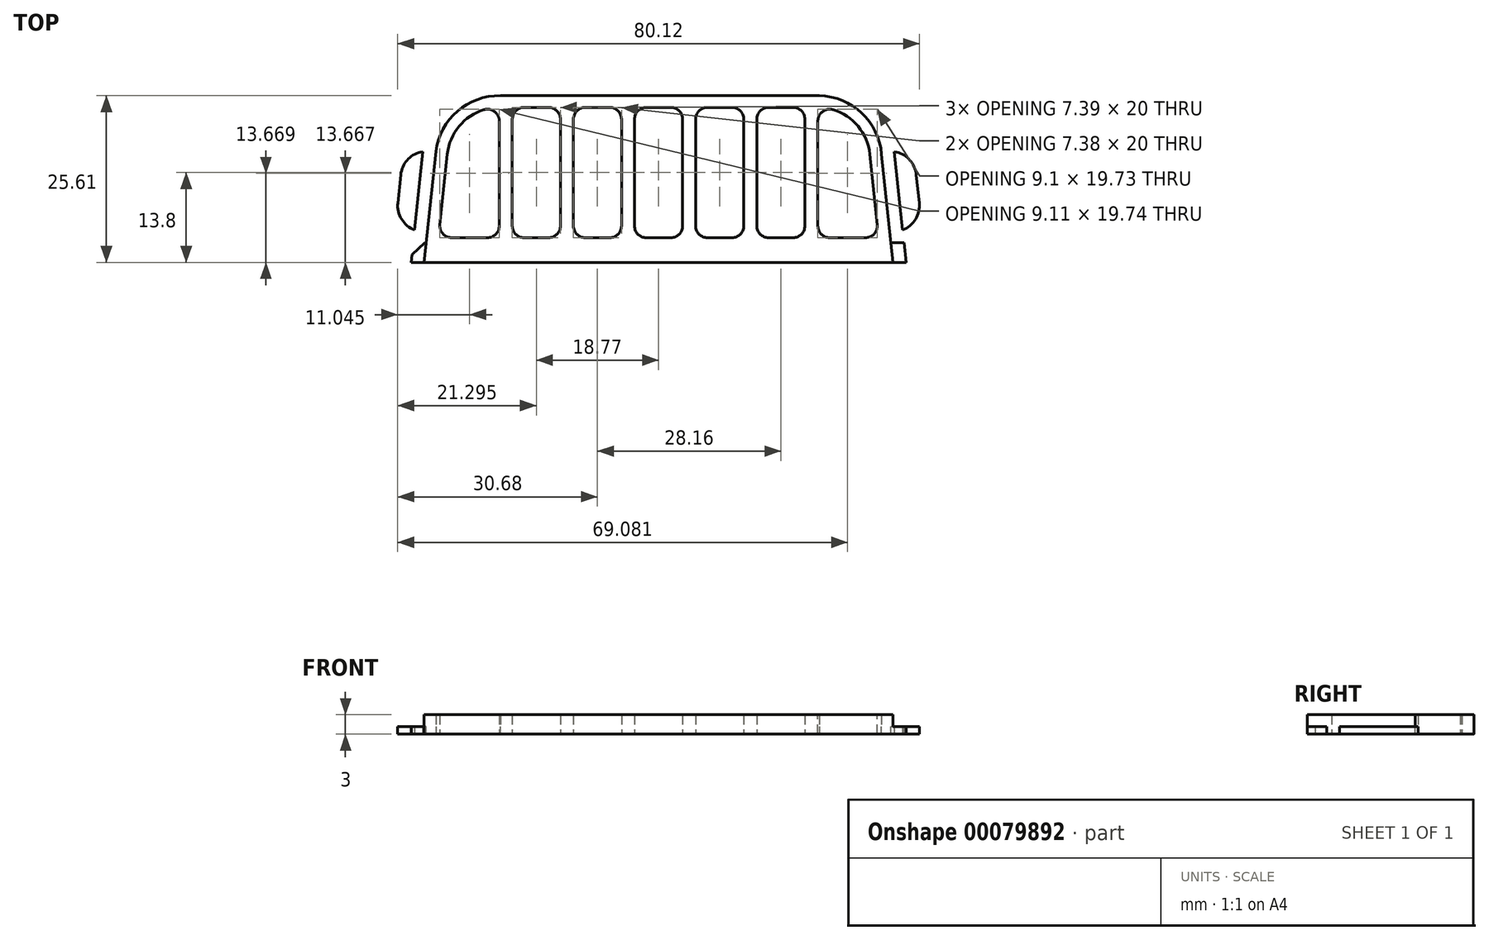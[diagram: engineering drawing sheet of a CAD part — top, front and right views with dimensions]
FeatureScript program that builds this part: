
annotation { "Feature Type Name" : "Feature", "Feature Type Description" : "" }
export const myFeature = defineFeature(function(context is Context, id is Id, definition is map)
    precondition{}
    {
        {
            var Q0;
            Q0=qCreatedBy(makeId("Top.planeOp"),FACE);
            var sketch = newSketch(context, id + "F0", { "sketchPlane" : qUnion([Q0])});
            skLineSegment(sketch, "E0", {"start": v(-36, 0) * mm, "end": v(36, 0) * mm});
            skLineSegment(sketch, "E1", {"start": v(-36, 24) * mm, "end": v(38.4, 24) * mm, "construction": true});
            skPoint(sketch, "E2", {"position": v(0, 0) * mm});
            skLineSegment(sketch, "E3", {"start": v(-36, 0) * mm, "end": v(-34.42, 15.05) * mm});
            skLineSegment(sketch, "E4.MirrorCS", {"start": v(36, 0) * mm, "end": v(34.42, 15.05) * mm});
            skLineSegment(sketch, "E5", {"start": v(24.47, 24) * mm, "end": v(-24.47, 24) * mm});
            skPoint(sketch, "E6.visualSharp", {"position": v(33.48, 24) * mm});
            skArc(sketch, "E6.filletArc", {"start": v(34.42, 15.05) * mm, "mid": v(31.16, 21.43) * mm, "end": v(24.47, 24) * mm});
            skPoint(sketch, "E7.visualSharp", {"position": v(-33.48, 24) * mm});
            skArc(sketch, "E7.filletArc", {"start": v(-24.47, 24) * mm, "mid": v(-31.16, 21.43) * mm, "end": v(-34.42, 15.05) * mm});
            skSolve(sketch);
        }
        {
            var Q0;
            Q0=qCreatedBy(makeId("Top.planeOp"),FACE);
            var sketch = newSketch(context, id + "F1", { "sketchPlane" : qUnion([Q0])});
            skArc(sketch, "E8.0", {"start": v(36.2, 15.23) * mm, "mid": v(32.37, 22.77) * mm, "end": v(24.47, 25.8) * mm});
            skArc(sketch, "E8.1", {"start": v(-24.47, 25.8) * mm, "mid": v(-32.37, 22.77) * mm, "end": v(-36.2, 15.23) * mm});
            skLineSegment(sketch, "E8.2", {"start": v(-38, -1.8) * mm, "end": v(-36.2, 15.23) * mm});
            skLineSegment(sketch, "E8.3", {"start": v(24.47, 25.8) * mm, "end": v(-24.47, 25.8) * mm});
            skLineSegment(sketch, "E8.4", {"start": v(-38, -1.8) * mm, "end": v(38, -1.8) * mm});
            skLineSegment(sketch, "E8.5", {"start": v(38, -1.8) * mm, "end": v(36.2, 15.23) * mm});
            skSolve(sketch);
        }
        {
            var Q0;
            Q0=makeQuery(id+"F1.imprint","IMPRINT",FACE,{"disambiguationData":[TD([[makeQuery(id+"F1.imprint","IMPRINT",EDGE,{"derivedFrom":sQuery(id+"F1.wireOp",EDGE,"E8.0")}),1.0]])]});
            extrude(context, id + "F2", {"entities" : qUnion([Q0]), "depth" : 3 * mm});
        }
        {
            var Q0;
            Q0=makeQuery(id+"F2.opExtrude","SWEPT_FACE",FACE,{"disambiguationData":[OSD([sQuery(id+"F1.wireOp",EDGE,"E8.4")])]});
            var sketch = newSketch(context, id + "F3", { "sketchPlane" : qUnion([Q0])});
            skLineSegment(sketch, "E9.bottom", {"start": v(-38, 3) * mm, "end": v(-36, 3) * mm});
            skLineSegment(sketch, "E9.top", {"start": v(-38, 1.2) * mm, "end": v(-36, 1.2) * mm});
            skLineSegment(sketch, "E9.left", {"start": v(-38, 3) * mm, "end": v(-38, 1.2) * mm});
            skLineSegment(sketch, "E9.right", {"start": v(-36, 3) * mm, "end": v(-36, 1.2) * mm});
            skLineSegment(sketch, "E10.0", {"start": v(-36, 0) * mm, "end": v(-34.42, 0) * mm});
            skPoint(sketch, "E11", {"position": v(-38, 1.5) * mm});
            skSolve(sketch);
        }
        {
            var Q0;
            Q0=makeQuery(id+"F3.imprint","IMPRINT",FACE,{"disambiguationData":[TD([[makeQuery(id+"F3.imprint","IMPRINT",EDGE,{"derivedFrom":sQuery(id+"F3.wireOp",EDGE,"E9.bottom")}),-1.0]])]});
            var Q1;
            Q1=makeQuery(id+"F2.opExtrude","CAP_EDGE",EDGE,{"disambiguationData":[OSD([sQuery(id+"F1.wireOp",EDGE,"E8.2")])],"isStart":false});
            var Q2;
            Q2=makeQuery(id+"F2.opExtrude","CAP_EDGE",EDGE,{"disambiguationData":[OSD([sQuery(id+"F1.wireOp",EDGE,"E8.1")])],"isStart":false});
            var Q3;
            Q3=makeQuery(id+"F2.opExtrude","CAP_EDGE",EDGE,{"disambiguationData":[OSD([sQuery(id+"F1.wireOp",EDGE,"E8.3")])],"isStart":false});
            var Q4;
            Q4=makeQuery(id+"F2.opExtrude","CAP_EDGE",EDGE,{"disambiguationData":[OSD([sQuery(id+"F1.wireOp",EDGE,"E8.0")])],"isStart":false});
            var Q5;
            Q5=makeQuery(id+"F2.opExtrude","CAP_EDGE",EDGE,{"disambiguationData":[OSD([sQuery(id+"F1.wireOp",EDGE,"E8.5")])],"isStart":false});
            sweep(context, id + "F4", {"operationType" : NewBodyOperationType.REMOVE, "profiles" : qUnion([Q0]), "path" : qUnion([Q1, Q2, Q3, Q4, Q5])});
        }
        {
            var Q0;
            Q0=makeQuery(id+"F0.imprint","IMPRINT",FACE,{"disambiguationData":[TD([[makeQuery(id+"F0.imprint","IMPRINT",EDGE,{"derivedFrom":sQuery(id+"F0.wireOp",EDGE,"E0")}),1.0]])]});
            var sketch = newSketch(context, id + "F5", { "sketchPlane" : qUnion([Q0])});
            skLineSegment(sketch, "E12.0", {"start": v(-33.78, 2) * mm, "end": v(-32.43, 14.84) * mm});
            skLineSegment(sketch, "E12.1", {"start": v(33.78, 2) * mm, "end": v(32.43, 14.84) * mm});
            skArc(sketch, "E12.2", {"start": v(32.43, 14.84) * mm, "mid": v(29.83, 19.95) * mm, "end": v(24.47, 22) * mm});
            skLineSegment(sketch, "E12.3", {"start": v(-33.78, 2) * mm, "end": v(33.78, 2) * mm});
            skLineSegment(sketch, "E12.4", {"start": v(24.47, 22) * mm, "end": v(-24.47, 22) * mm});
            skArc(sketch, "E12.5", {"start": v(-24.47, 22) * mm, "mid": v(-29.83, 19.95) * mm, "end": v(-32.43, 14.84) * mm});
            skLineSegment(sketch, "E13.bottom", {"start": v(24.47, 22) * mm, "end": v(22.47, 22) * mm});
            skLineSegment(sketch, "E13.top", {"start": v(24.47, 2) * mm, "end": v(22.47, 2) * mm});
            skLineSegment(sketch, "E13.left", {"start": v(24.47, 22) * mm, "end": v(24.47, 2) * mm});
            skLineSegment(sketch, "E13.right", {"start": v(22.47, 22) * mm, "end": v(22.47, 2) * mm});
            skLineSegment(sketch, "E14.1.0.0", {"start": v(15.09, 22) * mm, "end": v(15.09, 2) * mm});
            skLineSegment(sketch, "E14.1.0.1", {"start": v(15.09, 2) * mm, "end": v(13.09, 2) * mm});
            skLineSegment(sketch, "E14.1.0.2", {"start": v(13.09, 22) * mm, "end": v(13.09, 2) * mm});
            skLineSegment(sketch, "E14.1.0.3", {"start": v(15.09, 22) * mm, "end": v(13.09, 22) * mm});
            skLineSegment(sketch, "E14.2.0.0", {"start": v(5.7, 22) * mm, "end": v(5.7, 2) * mm});
            skLineSegment(sketch, "E14.2.0.1", {"start": v(5.7, 2) * mm, "end": v(3.7, 2) * mm});
            skLineSegment(sketch, "E14.2.0.2", {"start": v(3.7, 22) * mm, "end": v(3.7, 2) * mm});
            skLineSegment(sketch, "E14.2.0.3", {"start": v(5.7, 22) * mm, "end": v(3.7, 22) * mm});
            skLineSegment(sketch, "E14.3.0.0", {"start": v(-3.69, 22) * mm, "end": v(-3.69, 2) * mm});
            skLineSegment(sketch, "E14.3.0.1", {"start": v(-3.69, 2) * mm, "end": v(-5.69, 2) * mm});
            skLineSegment(sketch, "E14.3.0.2", {"start": v(-5.69, 22) * mm, "end": v(-5.69, 2) * mm});
            skLineSegment(sketch, "E14.3.0.3", {"start": v(-3.69, 22) * mm, "end": v(-5.69, 22) * mm});
            skLineSegment(sketch, "E14.4.0.0", {"start": v(-13.07, 22) * mm, "end": v(-13.07, 2) * mm});
            skLineSegment(sketch, "E14.4.0.1", {"start": v(-13.07, 2) * mm, "end": v(-15.07, 2) * mm});
            skLineSegment(sketch, "E14.4.0.2", {"start": v(-15.07, 22) * mm, "end": v(-15.07, 2) * mm});
            skLineSegment(sketch, "E14.4.0.3", {"start": v(-13.07, 22) * mm, "end": v(-15.07, 22) * mm});
            skLineSegment(sketch, "E14.5.0.0", {"start": v(-22.46, 22) * mm, "end": v(-22.46, 2) * mm});
            skLineSegment(sketch, "E14.5.0.1", {"start": v(-22.46, 2) * mm, "end": v(-24.46, 2) * mm});
            skLineSegment(sketch, "E14.5.0.2", {"start": v(-24.46, 22) * mm, "end": v(-24.46, 2) * mm});
            skLineSegment(sketch, "E14.5.0.3", {"start": v(-22.46, 22) * mm, "end": v(-24.46, 22) * mm});
            skLineSegment(sketch, "E14.direction1", {"start": v(24.47, 2) * mm, "end": v(15.09, 2) * mm, "construction": true});
            skSolve(sketch);
        }
        {
            var Q0;
            {var subQ0=sQuery(id+"F5.wireOp",EDGE,"E12.1");Q0=makeQuery(id+"F5.imprint","IMPRINT",FACE,{"disambiguationData":[TD([[makeQuery(id+"F5.imprint","IMPRINT",EDGE,{"derivedFrom":subQ0}),1.0]])]});}
            var Q1;
            {var subQ0=sQuery(id+"F5.wireOp",EDGE,"E13.right");Q1=makeQuery(id+"F5.imprint","IMPRINT",FACE,{"disambiguationData":[TD([[makeQuery(id+"F5.imprint","IMPRINT",EDGE,{"derivedFrom":subQ0}),-1.0]])]});}
            var Q2;
            {var subQ0=sQuery(id+"F5.wireOp",EDGE,"E14.1.0.2");Q2=makeQuery(id+"F5.imprint","IMPRINT",FACE,{"disambiguationData":[TD([[makeQuery(id+"F5.imprint","IMPRINT",EDGE,{"derivedFrom":subQ0}),-1.0]])]});}
            var Q3;
            {var subQ0=sQuery(id+"F5.wireOp",EDGE,"E14.2.0.2");Q3=makeQuery(id+"F5.imprint","IMPRINT",FACE,{"disambiguationData":[TD([[makeQuery(id+"F5.imprint","IMPRINT",EDGE,{"derivedFrom":subQ0}),-1.0]])]});}
            var Q4;
            {var subQ0=sQuery(id+"F5.wireOp",EDGE,"E14.3.0.2");Q4=makeQuery(id+"F5.imprint","IMPRINT",FACE,{"disambiguationData":[TD([[makeQuery(id+"F5.imprint","IMPRINT",EDGE,{"derivedFrom":subQ0}),-1.0]])]});}
            var Q5;
            {var subQ0=sQuery(id+"F5.wireOp",EDGE,"E14.4.0.2");Q5=makeQuery(id+"F5.imprint","IMPRINT",FACE,{"disambiguationData":[TD([[makeQuery(id+"F5.imprint","IMPRINT",EDGE,{"derivedFrom":subQ0}),-1.0]])]});}
            var Q6;
            {var subQ4=sQuery(id+"F5.wireOp",EDGE,"E12.0");Q6=makeQuery(id+"F5.imprint","IMPRINT",FACE,{"disambiguationData":[TD([[makeQuery(id+"F5.imprint","IMPRINT",EDGE,{"derivedFrom":subQ4}),-1.0]])]});}
            extrude(context, id + "F6", {"entities" : qUnion([Q0, Q1, Q2, Q3, Q4, Q5, Q6]), "operationType" : NewBodyOperationType.REMOVE, "endBound" : BoundingType.THROUGH_ALL, "depth" : 25 * mm});
        }
        {
            var Q0;
            Q0=makeQuery(id+"F4.boolean.opBoolean","COPY",FACE,{"derivedFrom":makeQuery(id+"F4.opSweep","SWEPT_FACE",FACE,{"disambiguationData":[OSD([sQuery(id+"F1.wireOp",EDGE,"E8.2"),sQuery(id+"F3.wireOp",EDGE,"E9.top")])]})});
            var sketch = newSketch(context, id + "F7", { "sketchPlane" : qUnion([Q0])});
            skLineSegment(sketch, "E15", {"start": v(-37.68, 1.2) * mm, "end": v(-35.68, 1.2) * mm});
            skLineSegment(sketch, "E16", {"start": v(-35.68, 1.2) * mm, "end": v(-36, -1.8) * mm});
            skLineSegment(sketch, "E17", {"start": v(-36, -1.8) * mm, "end": v(-38, -1.8) * mm});
            skLineSegment(sketch, "E18", {"start": v(-38, -1.8) * mm, "end": v(-37.68, 1.2) * mm});
            skLineSegment(sketch, "E19.MirrorCS", {"start": v(38, -1.8) * mm, "end": v(37.68, 1.2) * mm});
            skLineSegment(sketch, "E20.MirrorCS", {"start": v(36, -1.8) * mm, "end": v(38, -1.8) * mm});
            skLineSegment(sketch, "E21.MirrorCS", {"start": v(37.68, 1.2) * mm, "end": v(35.68, 1.2) * mm});
            skLineSegment(sketch, "E22.MirrorCS", {"start": v(35.68, 1.2) * mm, "end": v(36, -1.8) * mm});
            skSolve(sketch);
        }
        {
            var Q0;
            Q0=makeQuery(id+"F7.imprint","IMPRINT",FACE,{"disambiguationData":[TD([[makeQuery(id+"F7.imprint","IMPRINT",EDGE,{"derivedFrom":sQuery(id+"F7.wireOp",EDGE,"E15")}),-1.0]])]});
            var Q1;
            Q1=makeQuery(id+"F7.imprint","IMPRINT",FACE,{"disambiguationData":[TD([[makeQuery(id+"F7.imprint","IMPRINT",EDGE,{"derivedFrom":sQuery(id+"F7.wireOp",EDGE,"E19.MirrorCS")}),-1.0]])]});
            extrude(context, id + "F8", {"entities" : qUnion([Q0, Q1]), "operationType" : NewBodyOperationType.REMOVE, "endBound" : BoundingType.THROUGH_ALL, "oppositeDirection" : true, "depth" : 25 * mm});
        }
        {
            var Q0;
            Q0=makeQuery(id+"F8.boolean.opBoolean","COPY",EDGE,{"derivedFrom":makeQuery(id+"F8.opExtrude","SWEPT_EDGE",EDGE,{"disambiguationData":[OSD([sQuery(id+"F1.wireOp",EDGE,"E8.2"),sQuery(id+"F1.wireOp",EDGE,"E8.4"),sQuery(id+"F3.wireOp",EDGE,"E9.top"),sQuery(id+"F3.wireOp",EDGE,"E9.left"),sQuery(id+"F7.wireOp",EDGE,"E15"),sQuery(id+"F7.wireOp",EDGE,"E18")])]})});
            var Q1;
            Q1=makeQuery(id+"F8.boolean.opBoolean","MERGE",EDGE,{"derivedFrom":[makeQuery(id+"F4.boolean.opBoolean","COPY",EDGE,{"derivedFrom":makeQuery(id+"F4.opSweep","CAP_EDGE",EDGE,{"disambiguationData":[OSD([sQuery(id+"F1.wireOp",EDGE,"E8.2"),sQuery(id+"F1.wireOp",EDGE,"E8.4"),sQuery(id+"F3.wireOp",EDGE,"E9.right")])],"isStart":true})}),makeQuery(id+"F8.opExtrude","SWEPT_EDGE",EDGE,{"disambiguationData":[OSD([sQuery(id+"F7.wireOp",EDGE,"E16"),sQuery(id+"F7.wireOp",EDGE,"E17")])]})]});
            var Q2;
            Q2=makeQuery(id+"F8.boolean.opBoolean","COPY",EDGE,{"derivedFrom":makeQuery(id+"F8.opExtrude","SWEPT_EDGE",EDGE,{"disambiguationData":[OSD([sQuery(id+"F1.wireOp",EDGE,"E8.2"),sQuery(id+"F1.wireOp",EDGE,"E8.4"),sQuery(id+"F1.wireOp",EDGE,"E8.5"),sQuery(id+"F3.wireOp",EDGE,"E9.top"),sQuery(id+"F3.wireOp",EDGE,"E9.left"),sQuery(id+"F7.wireOp",EDGE,"E19.MirrorCS"),sQuery(id+"F7.wireOp",EDGE,"E21.MirrorCS")])]})});
            var Q3;
            Q3=makeQuery(id+"F8.boolean.opBoolean","MERGE",EDGE,{"derivedFrom":[makeQuery(id+"F4.boolean.opBoolean","INTERSECT",EDGE,{"derivedFrom":[makeQuery(id+"F2.opExtrude","SWEPT_FACE",FACE,{"disambiguationData":[OSD([sQuery(id+"F1.wireOp",EDGE,"E8.4")])]}),makeQuery(id+"F4.opSweep","SWEPT_FACE",FACE,{"disambiguationData":[OSD([sQuery(id+"F1.wireOp",EDGE,"E8.5"),sQuery(id+"F3.wireOp",EDGE,"E9.right")])]})]}),makeQuery(id+"F8.opExtrude","SWEPT_EDGE",EDGE,{"disambiguationData":[OSD([sQuery(id+"F7.wireOp",EDGE,"E20.MirrorCS"),sQuery(id+"F7.wireOp",EDGE,"E22.MirrorCS")])]})]});
            chamfer(context, id + "F9", {"entities" : qUnion([Q0, Q1, Q2, Q3]), "width" : 2 * mm, "tangentPropagation" : true});
        }
        {
            var Q0;
            Q0=makeQuery(id+"F6.boolean.opBoolean","COPY",EDGE,{"derivedFrom":makeQuery(id+"F6.opExtrude","SWEPT_EDGE",EDGE,{"disambiguationData":[OSD([sQuery(id+"F5.wireOp",EDGE,"E12.4"),sQuery(id+"F5.wireOp",EDGE,"E14.4.0.2"),sQuery(id+"F5.wireOp",EDGE,"E14.4.0.3")])]})});
            var Q1;
            Q1=makeQuery(id+"F6.boolean.opBoolean","COPY",EDGE,{"derivedFrom":makeQuery(id+"F6.opExtrude","SWEPT_EDGE",EDGE,{"disambiguationData":[OSD([sQuery(id+"F5.wireOp",EDGE,"E12.4"),sQuery(id+"F5.wireOp",EDGE,"E14.3.0.2"),sQuery(id+"F5.wireOp",EDGE,"E14.3.0.3")])]})});
            var Q2;
            Q2=makeQuery(id+"F6.boolean.opBoolean","COPY",EDGE,{"derivedFrom":makeQuery(id+"F6.opExtrude","SWEPT_EDGE",EDGE,{"disambiguationData":[OSD([sQuery(id+"F5.wireOp",EDGE,"E12.4"),sQuery(id+"F5.wireOp",EDGE,"E14.2.0.2"),sQuery(id+"F5.wireOp",EDGE,"E14.2.0.3")])]})});
            var Q3;
            Q3=makeQuery(id+"F6.boolean.opBoolean","COPY",EDGE,{"derivedFrom":makeQuery(id+"F6.opExtrude","SWEPT_EDGE",EDGE,{"disambiguationData":[OSD([sQuery(id+"F5.wireOp",EDGE,"E12.4"),sQuery(id+"F5.wireOp",EDGE,"E14.1.0.2"),sQuery(id+"F5.wireOp",EDGE,"E14.1.0.3")])]})});
            var Q4;
            Q4=makeQuery(id+"F6.boolean.opBoolean","COPY",EDGE,{"derivedFrom":makeQuery(id+"F6.opExtrude","SWEPT_EDGE",EDGE,{"disambiguationData":[OSD([sQuery(id+"F5.wireOp",EDGE,"E12.4"),sQuery(id+"F5.wireOp",EDGE,"E13.bottom"),sQuery(id+"F5.wireOp",EDGE,"E13.right")])]})});
            var Q5;
            Q5=makeQuery(id+"F6.boolean.opBoolean","COPY",EDGE,{"derivedFrom":makeQuery(id+"F6.opExtrude","SWEPT_EDGE",EDGE,{"disambiguationData":[OSD([sQuery(id+"F5.wireOp",EDGE,"E12.1"),sQuery(id+"F5.wireOp",EDGE,"E12.3")])]})});
            var Q6;
            Q6=makeQuery(id+"F6.boolean.opBoolean","COPY",EDGE,{"derivedFrom":makeQuery(id+"F6.opExtrude","SWEPT_EDGE",EDGE,{"disambiguationData":[OSD([sQuery(id+"F5.wireOp",EDGE,"E12.3"),sQuery(id+"F5.wireOp",EDGE,"E13.top"),sQuery(id+"F5.wireOp",EDGE,"E13.right")])]})});
            var Q7;
            Q7=makeQuery(id+"F6.boolean.opBoolean","COPY",EDGE,{"derivedFrom":makeQuery(id+"F6.opExtrude","SWEPT_EDGE",EDGE,{"disambiguationData":[OSD([sQuery(id+"F5.wireOp",EDGE,"E12.3"),sQuery(id+"F5.wireOp",EDGE,"E14.1.0.1"),sQuery(id+"F5.wireOp",EDGE,"E14.1.0.2")])]})});
            var Q8;
            Q8=makeQuery(id+"F6.boolean.opBoolean","COPY",EDGE,{"derivedFrom":makeQuery(id+"F6.opExtrude","SWEPT_EDGE",EDGE,{"disambiguationData":[OSD([sQuery(id+"F5.wireOp",EDGE,"E12.3"),sQuery(id+"F5.wireOp",EDGE,"E14.2.0.1"),sQuery(id+"F5.wireOp",EDGE,"E14.2.0.2")])]})});
            var Q9;
            Q9=makeQuery(id+"F6.boolean.opBoolean","COPY",EDGE,{"derivedFrom":makeQuery(id+"F6.opExtrude","SWEPT_EDGE",EDGE,{"disambiguationData":[OSD([sQuery(id+"F5.wireOp",EDGE,"E12.3"),sQuery(id+"F5.wireOp",EDGE,"E14.3.0.1"),sQuery(id+"F5.wireOp",EDGE,"E14.3.0.2")])]})});
            var Q10;
            Q10=makeQuery(id+"F6.boolean.opBoolean","COPY",EDGE,{"derivedFrom":makeQuery(id+"F6.opExtrude","SWEPT_EDGE",EDGE,{"disambiguationData":[OSD([sQuery(id+"F5.wireOp",EDGE,"E12.3"),sQuery(id+"F5.wireOp",EDGE,"E14.4.0.1"),sQuery(id+"F5.wireOp",EDGE,"E14.4.0.2")])]})});
            var Q11;
            Q11=makeQuery(id+"F6.boolean.opBoolean","COPY",EDGE,{"derivedFrom":makeQuery(id+"F6.opExtrude","SWEPT_EDGE",EDGE,{"disambiguationData":[OSD([sQuery(id+"F5.wireOp",EDGE,"E12.3"),sQuery(id+"F5.wireOp",EDGE,"E14.5.0.1"),sQuery(id+"F5.wireOp",EDGE,"E14.5.0.2")])]})});
            var Q12;
            Q12=makeQuery(id+"F6.boolean.opBoolean","COPY",EDGE,{"derivedFrom":makeQuery(id+"F6.opExtrude","SWEPT_EDGE",EDGE,{"disambiguationData":[OSD([sQuery(id+"F5.wireOp",EDGE,"E12.0"),sQuery(id+"F5.wireOp",EDGE,"E12.3")])]})});
            var Q13;
            Q13=makeQuery(id+"F6.boolean.opBoolean","COPY",EDGE,{"derivedFrom":makeQuery(id+"F6.opExtrude","SWEPT_EDGE",EDGE,{"disambiguationData":[OSD([sQuery(id+"F5.wireOp",EDGE,"E12.3"),sQuery(id+"F5.wireOp",EDGE,"E14.5.0.0"),sQuery(id+"F5.wireOp",EDGE,"E14.5.0.1")])]})});
            var Q14;
            Q14=makeQuery(id+"F6.boolean.opBoolean","COPY",EDGE,{"derivedFrom":makeQuery(id+"F6.opExtrude","SWEPT_EDGE",EDGE,{"disambiguationData":[OSD([sQuery(id+"F5.wireOp",EDGE,"E12.3"),sQuery(id+"F5.wireOp",EDGE,"E14.4.0.0"),sQuery(id+"F5.wireOp",EDGE,"E14.4.0.1")])]})});
            var Q15;
            Q15=makeQuery(id+"F6.boolean.opBoolean","COPY",EDGE,{"derivedFrom":makeQuery(id+"F6.opExtrude","SWEPT_EDGE",EDGE,{"disambiguationData":[OSD([sQuery(id+"F5.wireOp",EDGE,"E12.3"),sQuery(id+"F5.wireOp",EDGE,"E14.3.0.0"),sQuery(id+"F5.wireOp",EDGE,"E14.3.0.1")])]})});
            var Q16;
            Q16=makeQuery(id+"F6.boolean.opBoolean","COPY",EDGE,{"derivedFrom":makeQuery(id+"F6.opExtrude","SWEPT_EDGE",EDGE,{"disambiguationData":[OSD([sQuery(id+"F5.wireOp",EDGE,"E12.3"),sQuery(id+"F5.wireOp",EDGE,"E14.2.0.0"),sQuery(id+"F5.wireOp",EDGE,"E14.2.0.1")])]})});
            var Q17;
            Q17=makeQuery(id+"F6.boolean.opBoolean","COPY",EDGE,{"derivedFrom":makeQuery(id+"F6.opExtrude","SWEPT_EDGE",EDGE,{"disambiguationData":[OSD([sQuery(id+"F5.wireOp",EDGE,"E12.3"),sQuery(id+"F5.wireOp",EDGE,"E14.1.0.0"),sQuery(id+"F5.wireOp",EDGE,"E14.1.0.1")])]})});
            var Q18;
            Q18=makeQuery(id+"F6.boolean.opBoolean","COPY",EDGE,{"derivedFrom":makeQuery(id+"F6.opExtrude","SWEPT_EDGE",EDGE,{"disambiguationData":[OSD([sQuery(id+"F5.wireOp",EDGE,"E12.3"),sQuery(id+"F5.wireOp",EDGE,"E13.top"),sQuery(id+"F5.wireOp",EDGE,"E13.left")])]})});
            var Q19;
            Q19=makeQuery(id+"F6.boolean.opBoolean","COPY",EDGE,{"derivedFrom":makeQuery(id+"F6.opExtrude","SWEPT_EDGE",EDGE,{"disambiguationData":[OSD([sQuery(id+"F5.wireOp",EDGE,"E12.2"),sQuery(id+"F5.wireOp",EDGE,"E13.bottom"),sQuery(id+"F5.wireOp",EDGE,"E13.left")])]})});
            var Q20;
            Q20=makeQuery(id+"F6.boolean.opBoolean","COPY",EDGE,{"derivedFrom":makeQuery(id+"F6.opExtrude","SWEPT_EDGE",EDGE,{"disambiguationData":[OSD([sQuery(id+"F5.wireOp",EDGE,"E12.4"),sQuery(id+"F5.wireOp",EDGE,"E14.1.0.0"),sQuery(id+"F5.wireOp",EDGE,"E14.1.0.3")])]})});
            var Q21;
            Q21=makeQuery(id+"F6.boolean.opBoolean","COPY",EDGE,{"derivedFrom":makeQuery(id+"F6.opExtrude","SWEPT_EDGE",EDGE,{"disambiguationData":[OSD([sQuery(id+"F5.wireOp",EDGE,"E12.4"),sQuery(id+"F5.wireOp",EDGE,"E14.2.0.0"),sQuery(id+"F5.wireOp",EDGE,"E14.2.0.3")])]})});
            var Q22;
            Q22=makeQuery(id+"F6.boolean.opBoolean","COPY",EDGE,{"derivedFrom":makeQuery(id+"F6.opExtrude","SWEPT_EDGE",EDGE,{"disambiguationData":[OSD([sQuery(id+"F5.wireOp",EDGE,"E12.4"),sQuery(id+"F5.wireOp",EDGE,"E14.3.0.0"),sQuery(id+"F5.wireOp",EDGE,"E14.3.0.3")])]})});
            var Q23;
            Q23=makeQuery(id+"F6.boolean.opBoolean","COPY",EDGE,{"derivedFrom":makeQuery(id+"F6.opExtrude","SWEPT_EDGE",EDGE,{"disambiguationData":[OSD([sQuery(id+"F5.wireOp",EDGE,"E12.4"),sQuery(id+"F5.wireOp",EDGE,"E14.4.0.0"),sQuery(id+"F5.wireOp",EDGE,"E14.4.0.3")])]})});
            var Q24;
            Q24=makeQuery(id+"F6.boolean.opBoolean","COPY",EDGE,{"derivedFrom":makeQuery(id+"F6.opExtrude","SWEPT_EDGE",EDGE,{"disambiguationData":[OSD([sQuery(id+"F5.wireOp",EDGE,"E12.4"),sQuery(id+"F5.wireOp",EDGE,"E14.5.0.0"),sQuery(id+"F5.wireOp",EDGE,"E14.5.0.3")])]})});
            var Q25;
            Q25=makeQuery(id+"F6.boolean.opBoolean","COPY",EDGE,{"derivedFrom":makeQuery(id+"F6.opExtrude","SWEPT_EDGE",EDGE,{"disambiguationData":[OSD([sQuery(id+"F5.wireOp",EDGE,"E12.4"),sQuery(id+"F5.wireOp",EDGE,"E14.5.0.2"),sQuery(id+"F5.wireOp",EDGE,"E14.5.0.3")])]})});
            fillet(context, id + "F10", {"entities" : qUnion([Q0, Q1, Q2, Q3, Q4, Q5, Q6, Q7, Q8, Q9, Q10, Q11, Q12, Q13, Q14, Q15, Q16, Q17, Q18, Q19, Q20, Q21, Q22, Q23, Q24, Q25]), "radius" : 1.8 * mm, "tangentPropagation" : true, "allowEdgeOverflow" : false});
        }
        {
            var Q0;
            Q0=qCreatedBy(makeId("Top.planeOp"),FACE);
            var sketch = newSketch(context, id + "F11", { "sketchPlane" : qUnion([Q0])});
            skLineSegment(sketch, "E23", {"start": v(-36.2, 15.23) * mm, "end": v(-39.29, 14.47) * mm});
            skLineSegment(sketch, "E24", {"start": v(-39.29, 14.47) * mm, "end": v(-40.47, 3.19) * mm});
            skLineSegment(sketch, "E25", {"start": v(-40.47, 3.19) * mm, "end": v(-37.47, 3.19) * mm});
            skLineSegment(sketch, "E26", {"start": v(-37.47, 3.19) * mm, "end": v(-36.2, 15.23) * mm});
            skLineSegment(sketch, "E27.MirrorCS", {"start": v(40.47, 3.19) * mm, "end": v(37.47, 3.19) * mm});
            skLineSegment(sketch, "E28.MirrorCS", {"start": v(39.29, 14.47) * mm, "end": v(40.47, 3.19) * mm});
            skLineSegment(sketch, "E29.MirrorCS", {"start": v(37.47, 3.19) * mm, "end": v(36.2, 15.23) * mm});
            skLineSegment(sketch, "E30.MirrorCS", {"start": v(36.2, 15.23) * mm, "end": v(39.29, 14.47) * mm});
            skSolve(sketch);
        }
        {
            var Q0;
            Q0=makeQuery(id+"F11.imprint","IMPRINT",FACE,{"disambiguationData":[TD([[makeQuery(id+"F11.imprint","IMPRINT",EDGE,{"derivedFrom":sQuery(id+"F11.wireOp",EDGE,"E23")}),1.0]])]});
            var Q1;
            Q1=makeQuery(id+"F11.imprint","IMPRINT",FACE,{"disambiguationData":[TD([[makeQuery(id+"F11.imprint","IMPRINT",EDGE,{"derivedFrom":sQuery(id+"F11.wireOp",EDGE,"E27.MirrorCS")}),-1.0]])]});
            var Q2;
            Q2=makeQuery(id+"F4.boolean.opBoolean","COPY",FACE,{"derivedFrom":makeQuery(id+"F4.opSweep","SWEPT_FACE",FACE,{"disambiguationData":[OSD([sQuery(id+"F1.wireOp",EDGE,"E8.2"),sQuery(id+"F3.wireOp",EDGE,"E9.top")])]})});
            extrude(context, id + "F12", {"entities" : qUnion([Q0, Q1]), "operationType" : NewBodyOperationType.ADD, "endBound" : BoundingType.UP_TO_SURFACE, "endBoundEntityFace" : qUnion([Q2]), "depth" : 25 * mm});
        }
        {
            var Q0;
            Q0=makeQuery(id+"F12.opExtrude","SWEPT_EDGE",EDGE,{"disambiguationData":[OSD([sQuery(id+"F11.wireOp",EDGE,"E24"),sQuery(id+"F11.wireOp",EDGE,"E25")])]});
            var Q1;
            Q1=makeQuery(id+"F12.opExtrude","SWEPT_EDGE",EDGE,{"disambiguationData":[OSD([sQuery(id+"F11.wireOp",EDGE,"E27.MirrorCS"),sQuery(id+"F11.wireOp",EDGE,"E28.MirrorCS")])]});
            var Q2;
            Q2=makeQuery(id+"F12.opExtrude","SWEPT_EDGE",EDGE,{"disambiguationData":[OSD([sQuery(id+"F11.wireOp",EDGE,"E23"),sQuery(id+"F11.wireOp",EDGE,"E24")])]});
            var Q3;
            Q3=makeQuery(id+"F12.opExtrude","SWEPT_EDGE",EDGE,{"disambiguationData":[OSD([sQuery(id+"F11.wireOp",EDGE,"E28.MirrorCS"),sQuery(id+"F11.wireOp",EDGE,"E30.MirrorCS")])]});
            fillet(context, id + "F13", {"entities" : qUnion([Q0, Q1, Q2, Q3]), "radius" : 4 * mm, "tangentPropagation" : true, "allowEdgeOverflow" : false});
        }
    });
